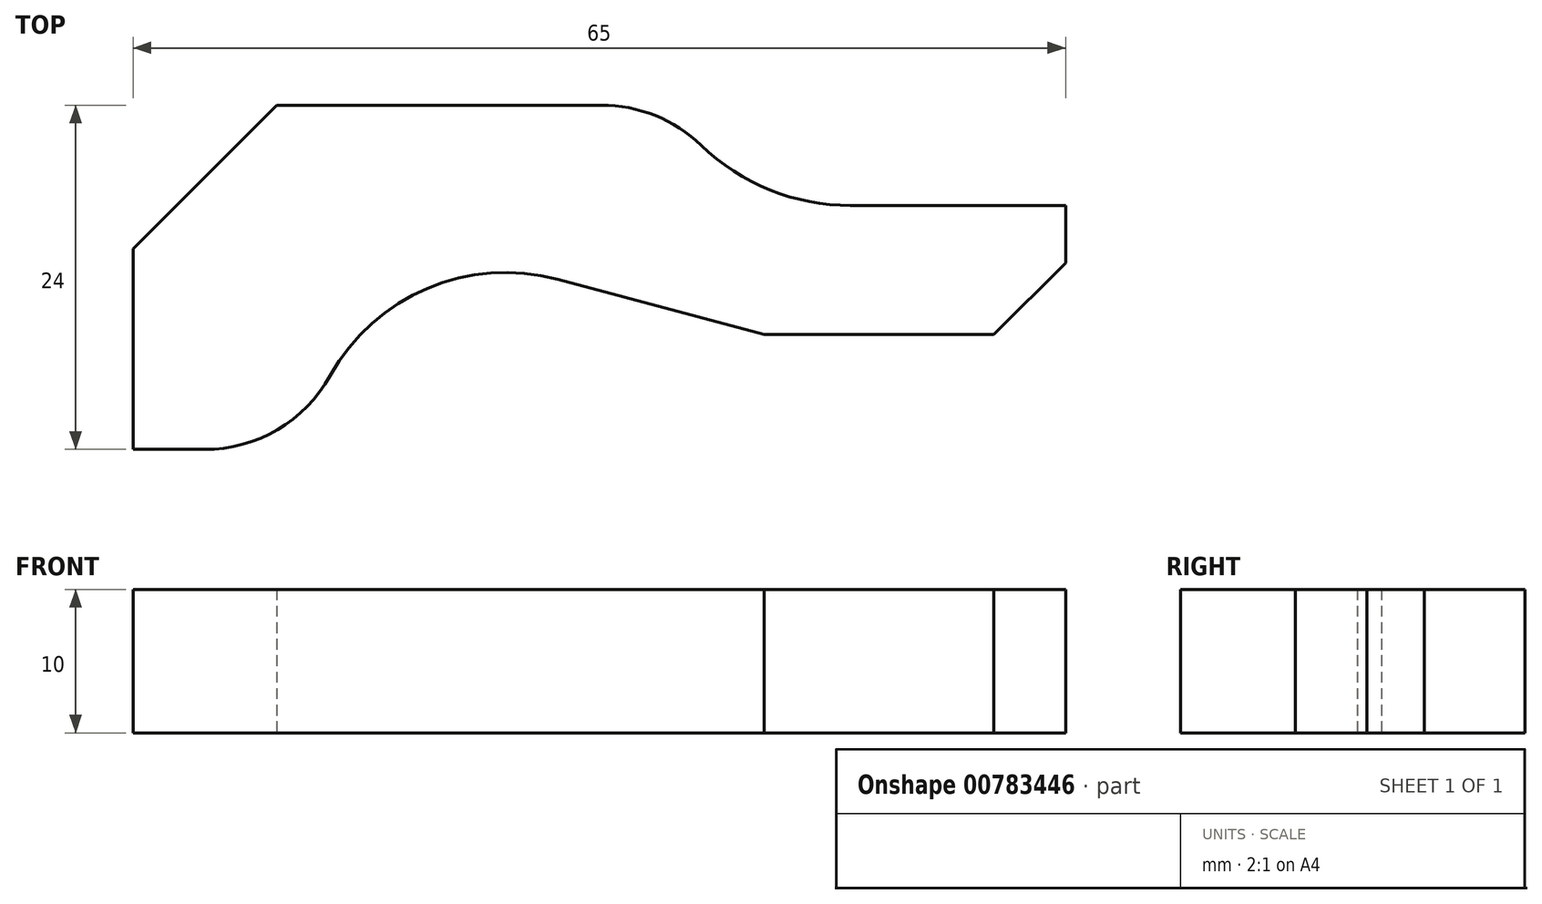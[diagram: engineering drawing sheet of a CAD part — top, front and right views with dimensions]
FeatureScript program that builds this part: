
annotation { "Feature Type Name" : "Feature", "Feature Type Description" : "" }
export const myFeature = defineFeature(function(context is Context, id is Id, definition is map)
    precondition{}
    {
        {
            var Q0;
            Q0=qCreatedBy(makeId("Top.planeOp"),FACE);
            var sketch = newSketch(context, id + "F0", { "sketchPlane" : qUnion([Q0])});
            skLineSegment(sketch, "E0", {"start": v(0, 0) * mm, "end": v(0, 14) * mm});
            skLineSegment(sketch, "E1", {"start": v(0, 14) * mm, "end": v(10, 24) * mm});
            skLineSegment(sketch, "E2", {"start": v(10, 24) * mm, "end": v(32.65, 24) * mm});
            skArc(sketch, "E3", {"start": v(32.65, 24) * mm, "mid": v(36.4, 23.27) * mm, "end": v(39.6, 21.2) * mm});
            skArc(sketch, "E4", {"start": v(39.6, 21.2) * mm, "mid": v(44.39, 18.09) * mm, "end": v(50, 17) * mm});
            skLineSegment(sketch, "E5", {"start": v(50, 17) * mm, "end": v(65, 17) * mm});
            skLineSegment(sketch, "E6", {"start": v(65, 17) * mm, "end": v(65, 13) * mm});
            skLineSegment(sketch, "E7", {"start": v(65, 13) * mm, "end": v(60, 8) * mm});
            skLineSegment(sketch, "E8", {"start": v(60, 8) * mm, "end": v(44, 8) * mm});
            skLineSegment(sketch, "E9", {"start": v(44, 8) * mm, "end": v(29.6, 11.86) * mm});
            skArc(sketch, "E10", {"start": v(29.6, 11.86) * mm, "mid": v(20.51, 11.23) * mm, "end": v(13.74, 5.14) * mm});
            skArc(sketch, "E11", {"start": v(13.74, 5.14) * mm, "mid": v(10.07, 1.38) * mm, "end": v(5, 0) * mm});
            skLineSegment(sketch, "E12", {"start": v(5, 0) * mm, "end": v(0, 0) * mm});
            skSolve(sketch);
        }
        {
            var Q0;
            Q0 = qSketchRegion(id + "F0", true);
            extrude(context, id + "F1", {"entities" : qUnion([Q0]), "depth" : 10 * mm, "offsetDistance" : 25 * mm});
        }
    });
